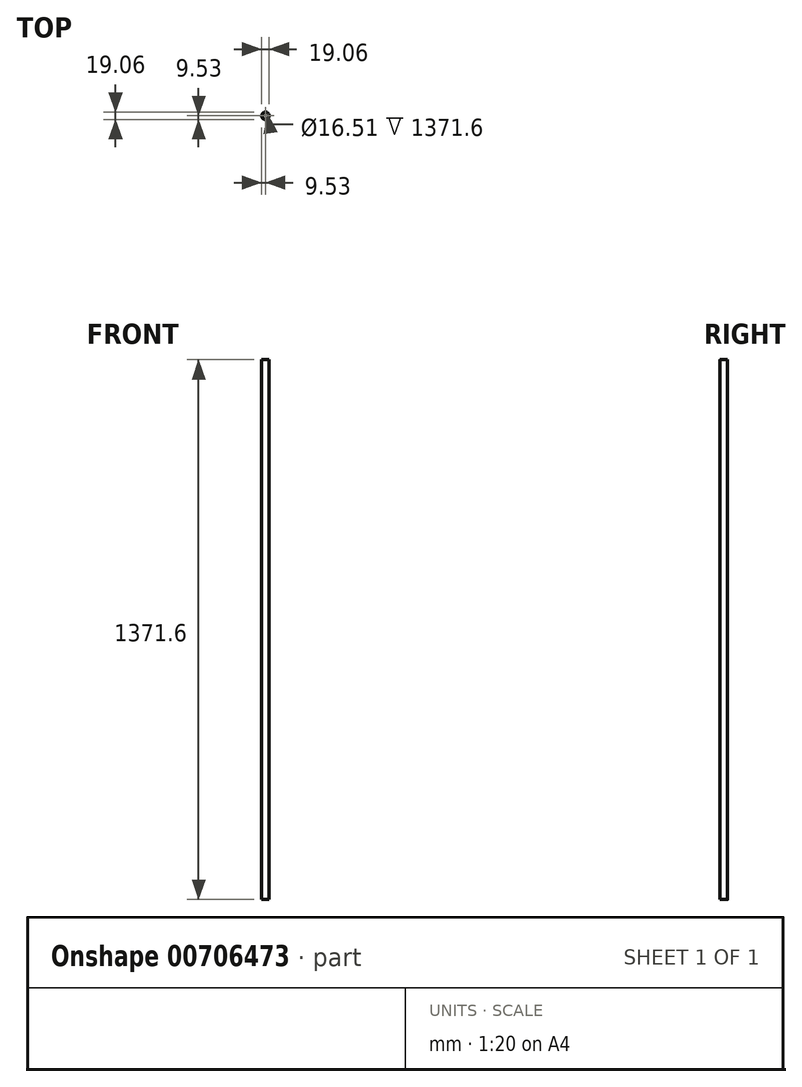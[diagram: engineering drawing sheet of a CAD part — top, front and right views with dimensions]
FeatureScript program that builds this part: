
annotation { "Feature Type Name" : "Feature", "Feature Type Description" : "" }
export const myFeature = defineFeature(function(context is Context, id is Id, definition is map)
    precondition{}
    {
        {
            var Q0;
            Q0=qCreatedBy(makeId("Top.planeOp"),FACE);
            var sketch = newSketch(context, id + "F0", { "sketchPlane" : qUnion([Q0])});
            skCircle(sketch, "E0", {"center": v(0, 0) * mm, "radius": 9.53 * mm});
            skCircle(sketch, "E1.0", {"center": v(0, 0) * mm, "radius": 8.26 * mm});
            skSolve(sketch);
        }
        {
            var Q0;
            Q0=makeQuery(id+"F0.imprint","IMPRINT",FACE,{"disambiguationData":[TD([[makeQuery(id+"F0.imprint","IMPRINT",EDGE,{"derivedFrom":sQuery(id+"F0.wireOp",EDGE,"E0")}),1.0]])]});
            extrude(context, id + "F1", {"entities" : qUnion([Q0]), "depth" : 1371.6 * mm, "offsetDistance" : 25.4 * mm});
        }
    });
